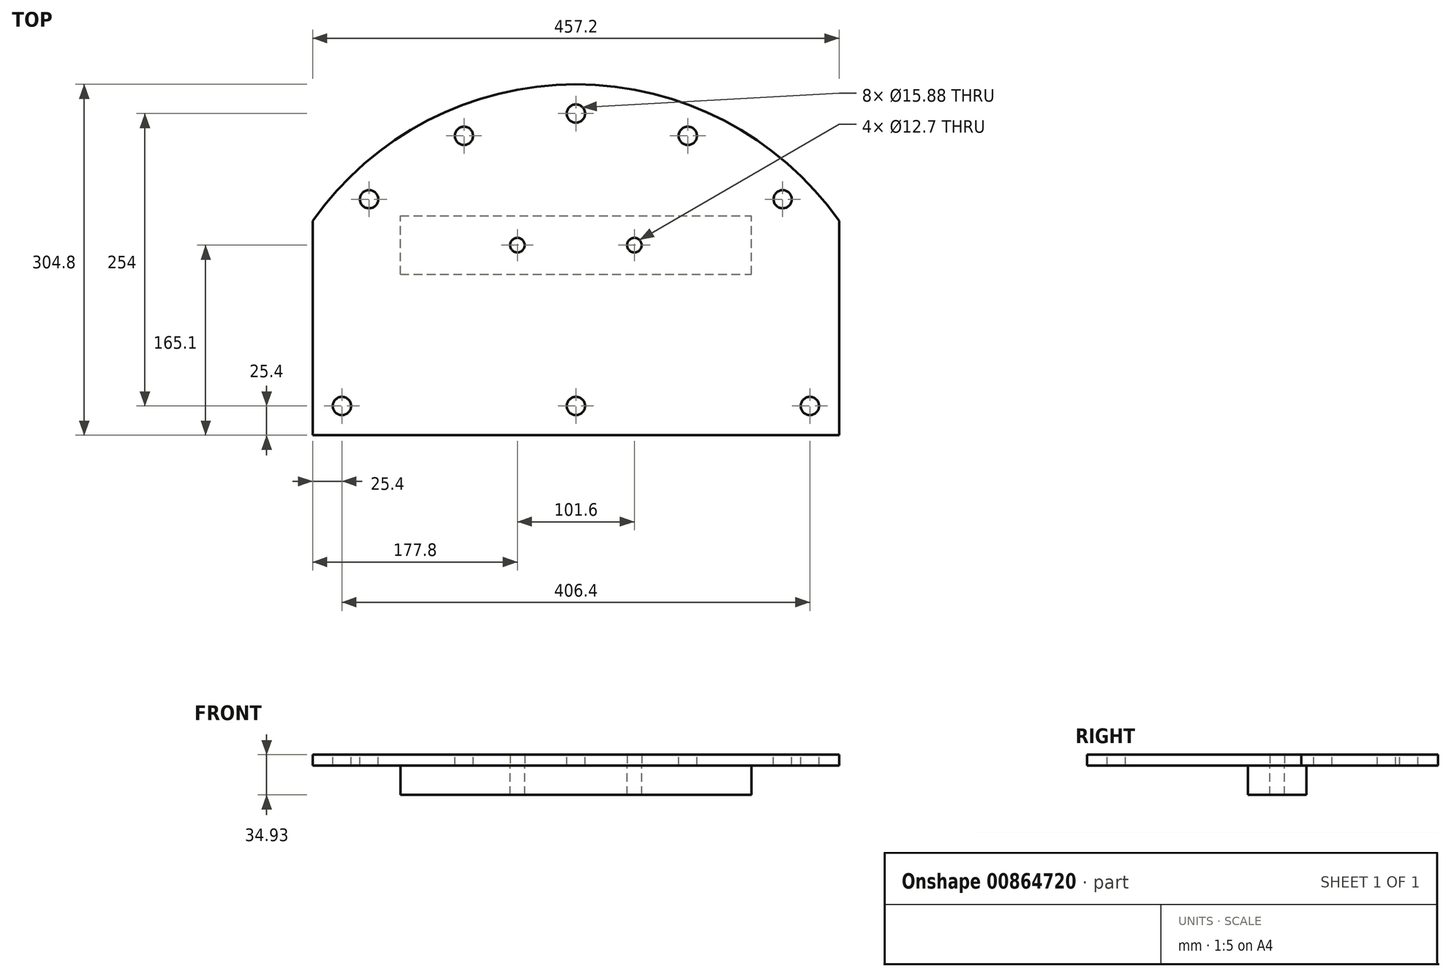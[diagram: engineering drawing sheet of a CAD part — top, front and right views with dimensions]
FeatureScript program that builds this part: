
annotation { "Feature Type Name" : "Feature", "Feature Type Description" : "" }
export const myFeature = defineFeature(function(context is Context, id is Id, definition is map)
    precondition{}
    {
        {
            var Q0;
            Q0=qCreatedBy(makeId("Top.planeOp"),FACE);
            var sketch = newSketch(context, id + "F0", { "sketchPlane" : qUnion([Q0])});
            skLineSegment(sketch, "E0.bottom", {"start": v(-228.6, -152.4) * mm, "end": v(228.6, -152.4) * mm});
            skLineSegment(sketch, "E0.left", {"start": v(-228.6, -152.4) * mm, "end": v(-228.6, 33.64) * mm});
            skLineSegment(sketch, "E0.right", {"start": v(228.6, -152.4) * mm, "end": v(228.6, 33.64) * mm});
            skPoint(sketch, "E0.middle", {"position": v(0, 0) * mm});
            skArc(sketch, "E1", {"start": v(-228.6, 33.64) * mm, "mid": v(0, 152.4) * mm, "end": v(228.6, 33.64) * mm});
            skCircle(sketch, "E2", {"center": v(97.2, 107.67) * mm, "radius": 7.94 * mm});
            skCircle(sketch, "E3", {"center": v(0, 127) * mm, "radius": 7.94 * mm});
            skCircle(sketch, "E4", {"center": v(179.6, 52.6) * mm, "radius": 7.94 * mm});
            skCircle(sketch, "E5", {"center": v(-203.2, -127) * mm, "radius": 7.94 * mm});
            skCircle(sketch, "E6", {"center": v(0, -127) * mm, "radius": 7.94 * mm});
            skCircle(sketch, "E7", {"center": v(203.2, -127) * mm, "radius": 7.94 * mm});
            skPoint(sketch, "E8.orphan", {"position": v(-228.6, 152.4) * mm});
            skPoint(sketch, "E9.orphan", {"position": v(228.6, 152.4) * mm});
            skCircle(sketch, "E10", {"center": v(-97.2, 107.67) * mm, "radius": 7.94 * mm});
            skCircle(sketch, "E11", {"center": v(-179.6, 52.6) * mm, "radius": 7.94 * mm});
            skSolve(sketch);
        }
        {
            var Q0;
            Q0=makeQuery(id+"F0.imprint","IMPRINT",FACE,{"disambiguationData":[TD([[makeQuery(id+"F0.imprint","IMPRINT",EDGE,{"derivedFrom":sQuery(id+"F0.wireOp",EDGE,"E0.bottom")}),1.0]])]});
            var Q1;
            Q1 = qSketchRegion(id + "Fct6jj6J449t4qU_1", true);
            extrude(context, id + "F1", {"entities" : qUnion([Q0, Q1]), "oppositeDirection" : true, "depth" : 9.52 * mm, "offsetDistance" : 25.4 * mm});
        }
        {
            var Q0;
            Q0=makeQuery(id+"F1.opExtrude","CAP_FACE",FACE,{"disambiguationData":[OSD([sQuery(id+"F0.wireOp",EDGE,"E0.bottom"),sQuery(id+"F0.wireOp",EDGE,"E0.left"),sQuery(id+"F0.wireOp",EDGE,"E0.right"),sQuery(id+"F0.wireOp",EDGE,"E1"),sQuery(id+"F0.wireOp",EDGE,"E2"),sQuery(id+"F0.wireOp",EDGE,"E3"),sQuery(id+"F0.wireOp",EDGE,"E4"),sQuery(id+"F0.wireOp",EDGE,"E5"),sQuery(id+"F0.wireOp",EDGE,"E6"),sQuery(id+"F0.wireOp",EDGE,"E7"),sQuery(id+"F0.wireOp",EDGE,"E10"),sQuery(id+"F0.wireOp",EDGE,"E11")])],"isStart":false});
            var sketch = newSketch(context, id + "F2", { "sketchPlane" : qUnion([Q0])});
            skLineSegment(sketch, "E12.bottom", {"start": v(-152.4, 12.7) * mm, "end": v(152.4, 12.7) * mm});
            skLineSegment(sketch, "E12.top", {"start": v(-152.4, -38.1) * mm, "end": v(152.4, -38.1) * mm});
            skLineSegment(sketch, "E12.left", {"start": v(-152.4, 12.7) * mm, "end": v(-152.4, -38.1) * mm});
            skLineSegment(sketch, "E12.right", {"start": v(152.4, 12.7) * mm, "end": v(152.4, -38.1) * mm});
            skPoint(sketch, "E12.middle", {"position": v(0, -12.7) * mm});
            skCircle(sketch, "E13", {"center": v(50.8, -12.7) * mm, "radius": 6.35 * mm});
            skCircle(sketch, "E14", {"center": v(-50.8, -12.7) * mm, "radius": 6.35 * mm});
            skSolve(sketch);
        }
        {
            var Q0;
            Q0=makeQuery(id+"F2.imprint","IMPRINT",FACE,{"disambiguationData":[TD([[makeQuery(id+"F2.imprint","IMPRINT",EDGE,{"derivedFrom":sQuery(id+"F2.wireOp",EDGE,"E12.top")}),1.0]])]});
            extrude(context, id + "F3", {"entities" : qUnion([Q0]), "depth" : 25.4 * mm, "offsetDistance" : 25.4 * mm});
        }
        {
            var Q0;
            Q0=makeQuery(id+"F2.imprint","IMPRINT",FACE,{"disambiguationData":[TD([[makeQuery(id+"F2.imprint","IMPRINT",EDGE,{"derivedFrom":sQuery(id+"F2.wireOp",EDGE,"E14")}),1.0]])]});
            var Q1;
            Q1=makeQuery(id+"F2.imprint","IMPRINT",FACE,{"disambiguationData":[TD([[makeQuery(id+"F2.imprint","IMPRINT",EDGE,{"derivedFrom":sQuery(id+"F2.wireOp",EDGE,"E13")}),1.0]])]});
            extrude(context, id + "F4", {"entities" : qUnion([Q0, Q1]), "operationType" : NewBodyOperationType.REMOVE, "endBound" : BoundingType.THROUGH_ALL, "oppositeDirection" : true, "depth" : 25.4 * mm, "offsetDistance" : 25.4 * mm});
        }
    });
